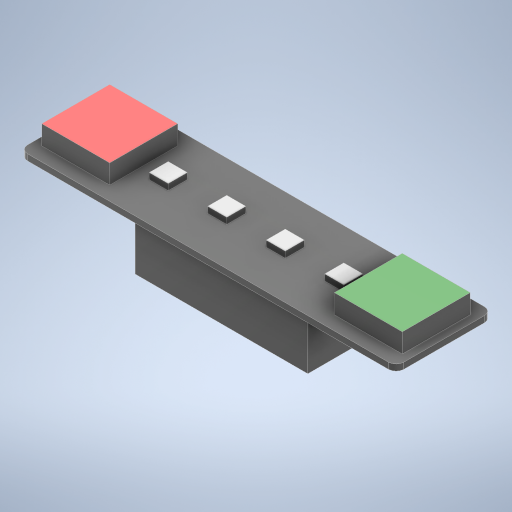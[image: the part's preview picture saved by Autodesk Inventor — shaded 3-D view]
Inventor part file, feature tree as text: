
AUTODESK INVENTOR PART (.ipt)
format: ipt  version: 2024.2 (Build 282272000, 272)  size: 350,720 bytes
history: native  units: mm
features: extrude x4, sketch x2, other x1
ambient origin geometry x8: Origin, YZ Plane, XZ Plane, XY Plane, X Axis, Y Axis, Z Axis, Center Point
bodies: Solid1 (feature_tree)
feature tree (7):
  other  "TorsoUpperFrame.ipt"
  sketch  "Sketch2"  dims[d3=5.0mm d4=0.0mm d5=16.6mm d6=0.0mm d7=1.6mm d8=0.0mm]
  extrude  "Extrusion1"  Depth=1.6mm TaperAngle=0.0deg
  extrude  "Extrusion2"  Depth=16.6mm TaperAngle=0.0deg
  extrude  "Extrusion3"  Depth=1.6mm TaperAngle=0.0deg
  extrude  "Extrusion4"  [1 undecoded]
  sketch  "Sketch1"  dims[d0=10.0mm d1=1.6mm d2=0.0mm]
note: 1 required parameter value undecoded (feature->parameter linkage not recoverable at this tier; creation-order binding heuristic only, values carry confidence <= 0.55)
